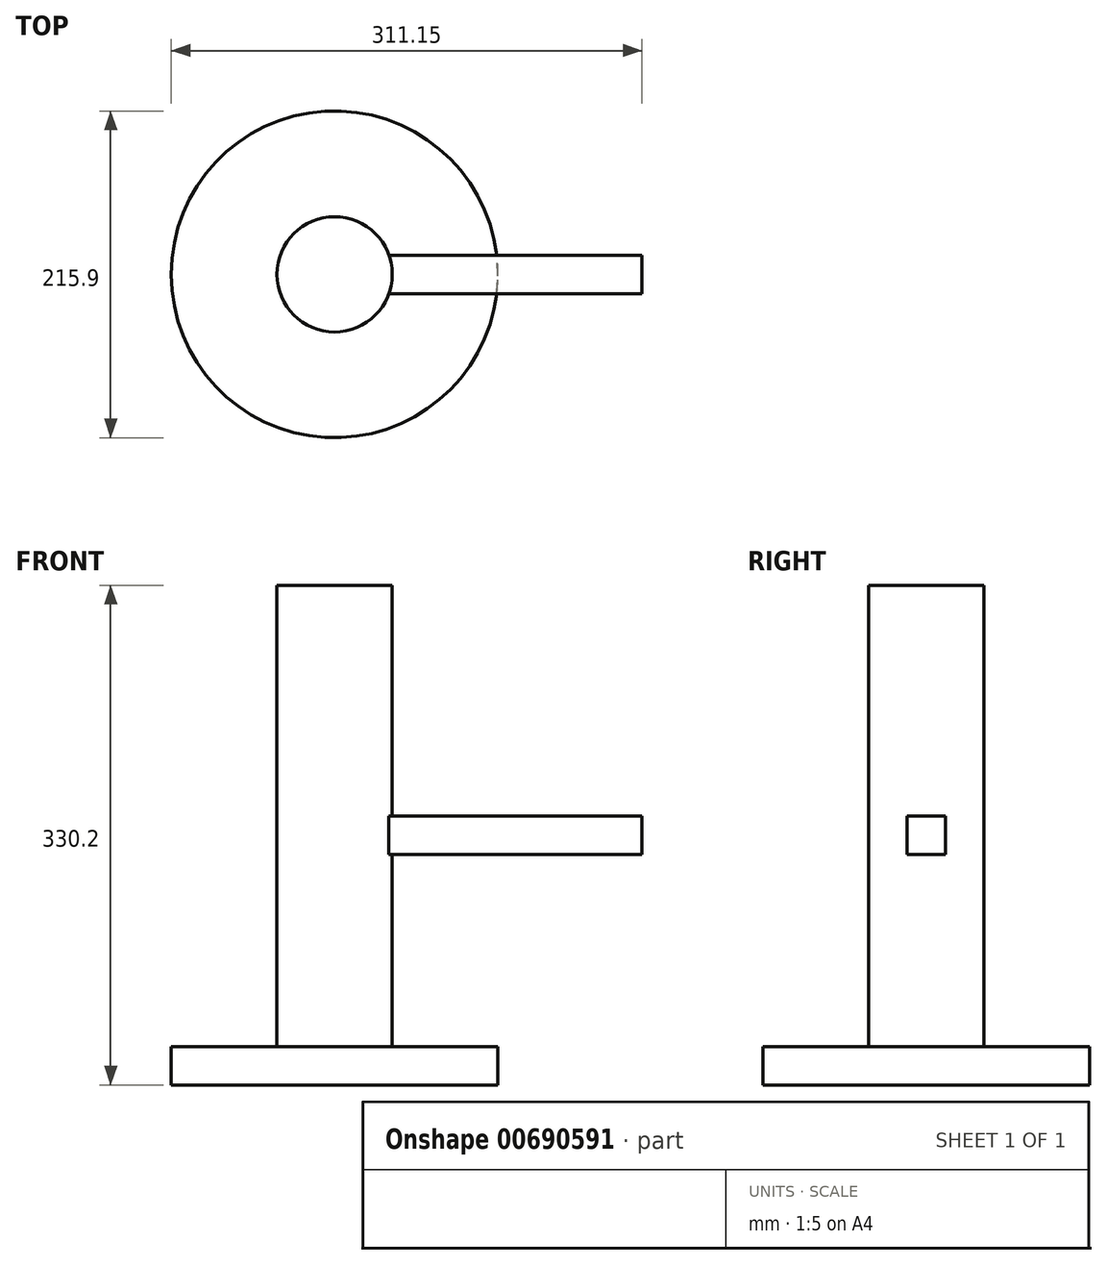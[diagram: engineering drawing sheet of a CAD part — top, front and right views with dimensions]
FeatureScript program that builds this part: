
annotation { "Feature Type Name" : "Feature", "Feature Type Description" : "" }
export const myFeature = defineFeature(function(context is Context, id is Id, definition is map)
    precondition{}
    {
        {
            var Q0;
            Q0=qCreatedBy(makeId("Top.planeOp"),FACE);
            var sketch = newSketch(context, id + "F0", { "sketchPlane" : qUnion([Q0])});
            skCircle(sketch, "E0", {"center": v(0, 0) * mm, "radius": 107.95 * mm});
            skSolve(sketch);
        }
        {
            var Q0;
            Q0 = qSketchRegion(id + "F0", true);
            extrude(context, id + "F1", {"entities" : qUnion([Q0]), "depth" : 25.4 * mm, "offsetDistance" : 25.4 * mm});
        }
        {
            var Q0;
            Q0=makeQuery(id+"F1.opExtrude","CAP_FACE",FACE,{"disambiguationData":[OSD([sQuery(id+"F0.wireOp",EDGE,"E0")])],"isStart":false});
            var sketch = newSketch(context, id + "F2", { "sketchPlane" : qUnion([Q0])});
            skCircle(sketch, "E1", {"center": v(0, 0) * mm, "radius": 38.1 * mm});
            skSolve(sketch);
        }
        {
            var Q0;
            Q0 = qSketchRegion(id + "F2", true);
            extrude(context, id + "F3", {"entities" : qUnion([Q0]), "operationType" : NewBodyOperationType.ADD, "depth" : 304.8 * mm, "offsetDistance" : 25.4 * mm});
        }
        {
            var Q0;
            Q0=qCreatedBy(makeId("Right.planeOp"),FACE);
            var sketch = newSketch(context, id + "F4", { "sketchPlane" : qUnion([Q0])});
            skLineSegment(sketch, "E2.bottom", {"start": v(-12.7, 152.4) * mm, "end": v(12.7, 152.4) * mm});
            skLineSegment(sketch, "E2.top", {"start": v(-12.7, 177.8) * mm, "end": v(12.7, 177.8) * mm});
            skLineSegment(sketch, "E2.left", {"start": v(-12.7, 152.4) * mm, "end": v(-12.7, 177.8) * mm});
            skLineSegment(sketch, "E2.right", {"start": v(12.7, 152.4) * mm, "end": v(12.7, 177.8) * mm});
            skSolve(sketch);
        }
        {
            var Q0;
            Q0 = qSketchRegion(id + "F4", true);
            extrude(context, id + "F5", {"entities" : qUnion([Q0]), "operationType" : NewBodyOperationType.ADD, "depth" : 203.2 * mm, "offsetDistance" : 25.4 * mm});
        }
    });
